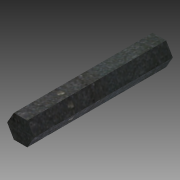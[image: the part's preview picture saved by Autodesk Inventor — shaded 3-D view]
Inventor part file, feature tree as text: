
AUTODESK INVENTOR PART (.ipt)
format: ipt  version: 2014 SP1 (Build 180222100, 222)  size: 86,528 bytes
history: native  units: in
note: dims shown in document units (in); Inventor stores cm internally (conversion verified against a paired STEP export)
features: extrude x1, sketch x1
ambient origin geometry x8: Origin, YZ Plane, XZ Plane, XY Plane, X Axis, Y Axis, Z Axis, Center Point
bodies: Solid1 (feature_tree)
feature tree (2):
  extrude  "Extrusion1"  Depth=3.0in TaperAngle=0.0deg
  sketch  "Sketch1"  dims[d0=0.5in d1=3.0in d2=0.0in]
